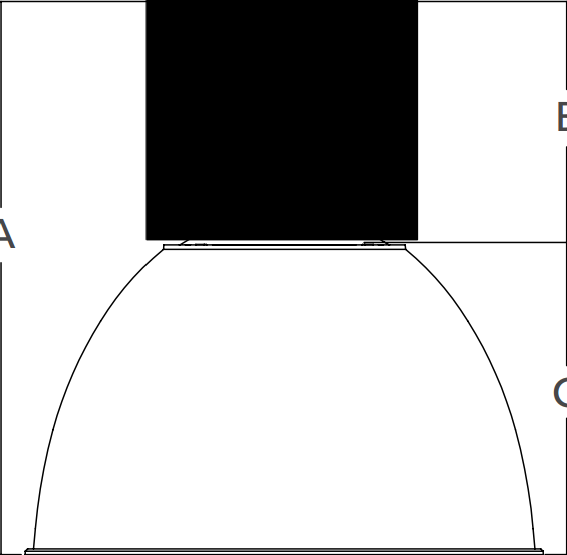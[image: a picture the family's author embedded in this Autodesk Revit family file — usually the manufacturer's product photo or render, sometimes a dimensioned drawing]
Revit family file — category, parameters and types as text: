
# Revit family: LBX2
name_source: partatom
category: Lighting Fixtures
revit_build: Autodesk Revit 2014 (Build: 20130308_1515(x64)
units: mm (PartAtom-declared; Revit-internal decimal feet)

## types (1)
- LBX2 - DB
    Apparent Load = 0 VA
    Assembly Code = D5020200
    Color Filter = 16777215
    Default Elevation = 48.000"
    Description = Lunabay2 Decorative LED Highbay
    Dimming Lamp Color Temperature Shift = <None>
    Emit Shape Visible in Rendering = No
    Emit from Circle Diameter = 8.000"
    Glass Material = Hubbell - White Glass
    Lamp = LED's
    Load Classification = Lighting
    Manufacturer = Hubbell Industrial Lighting
    Material Finish = Hubbell - White
    Model = LBX2
    Photometric Notes = More IES files Download on Photometric Web Link
    Photometric Web File = LBX2-LO-U-4K-A2-ND-AL23-WH.ies
    Photometric Web Link = https://www.hubbell.com
    Power Factor = 0.9
    Product Documentation Link = https://hubbellcdn.com
    Product Page URL = https://www.hubbell.com
    Tilt Angle = -90.00°
    Type Comments = Lighting Fixture
    URL = https://www.hubbell.com
    Voltage = 120 V
    Warranty = Five Years Warranty
    Watts = 102 W

## geometry (parser evidence)
native form markers: Blend x19, Sweep x2
no freeform markers — native parametric forms only
